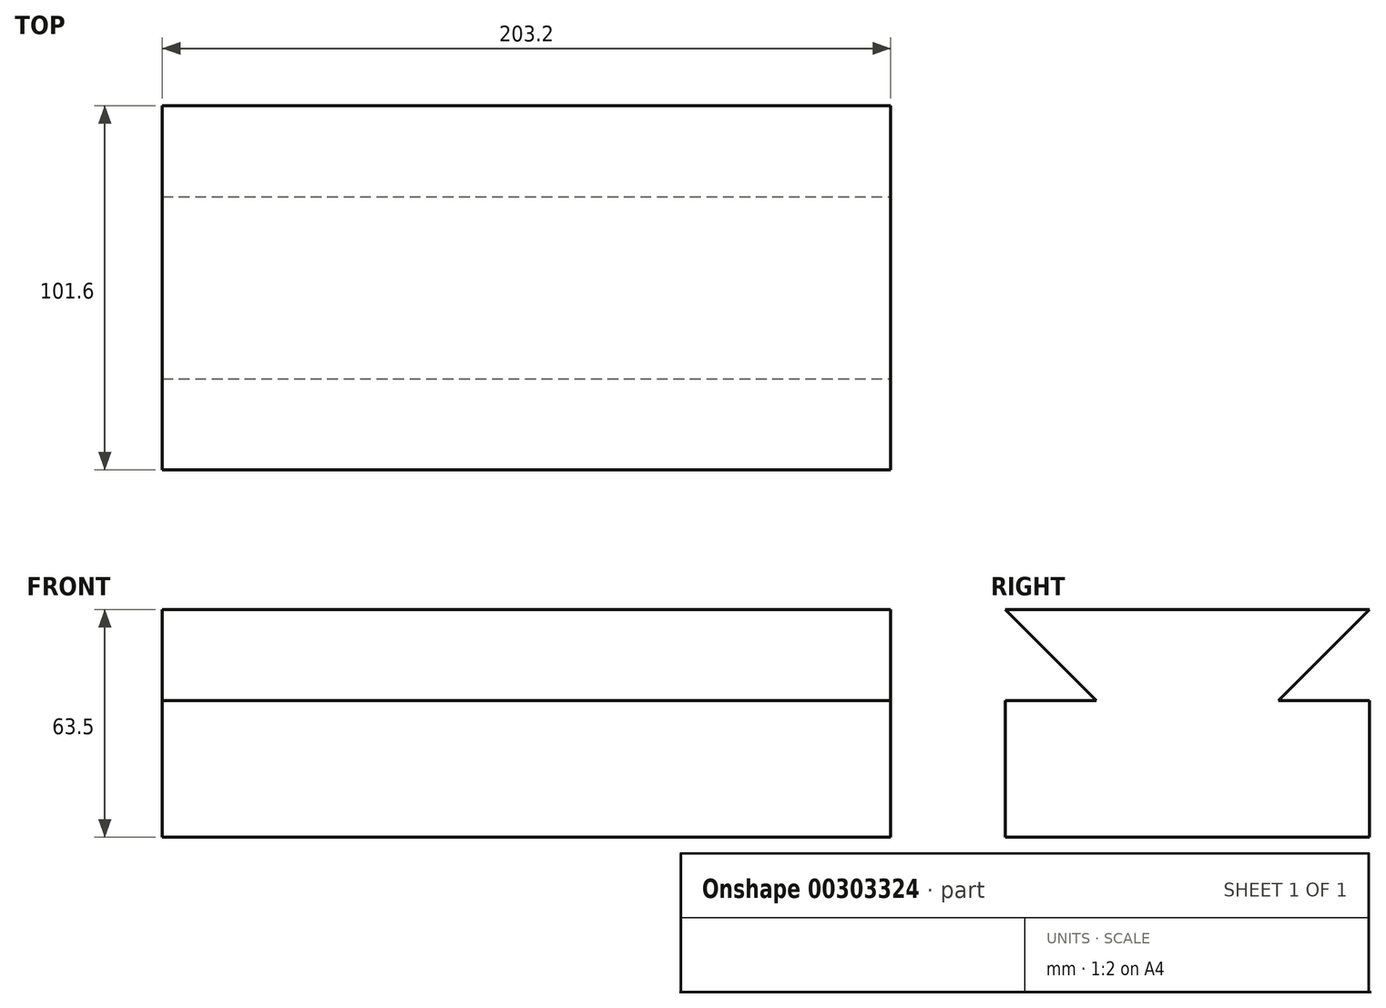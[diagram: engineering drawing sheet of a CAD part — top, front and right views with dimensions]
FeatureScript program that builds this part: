
annotation { "Feature Type Name" : "Feature", "Feature Type Description" : "" }
export const myFeature = defineFeature(function(context is Context, id is Id, definition is map)
    precondition{}
    {
        {
            var Q0;
            Q0=qCreatedBy(makeId("Right.planeOp"),FACE);
            var sketch = newSketch(context, id + "F0", { "sketchPlane" : qUnion([Q0])});
            skLineSegment(sketch, "E0.bottom", {"start": v(-35.6, 3.73) * mm, "end": v(66, 3.73) * mm});
            skLineSegment(sketch, "E0.top", {"start": v(-35.6, -59.77) * mm, "end": v(66, -59.77) * mm});
            skLineSegment(sketch, "E0.left", {"start": v(-35.6, 3.73) * mm, "end": v(-35.6, -59.77) * mm});
            skLineSegment(sketch, "E0.right", {"start": v(66, 3.73) * mm, "end": v(66, -59.77) * mm});
            skLineSegment(sketch, "E1", {"start": v(-35.6, 3.73) * mm, "end": v(-10.2, -21.67) * mm});
            skLineSegment(sketch, "E2", {"start": v(-10.2, -21.67) * mm, "end": v(-35.6, -21.67) * mm});
            skLineSegment(sketch, "E3", {"start": v(66, 3.73) * mm, "end": v(40.6, -21.67) * mm});
            skLineSegment(sketch, "E4", {"start": v(40.6, -21.67) * mm, "end": v(66, -21.67) * mm});
            skSolve(sketch);
        }
        {
            var Q0;
            Q0=makeQuery(id+"F0.imprint","IMPRINT",FACE,{"disambiguationData":[TD([[makeQuery(id+"F0.imprint","IMPRINT",EDGE,{"derivedFrom":sQuery(id+"F0.wireOp",EDGE,"E0.bottom")}),-1.0]])]});
            extrude(context, id + "F1", {"entities" : qUnion([Q0]), "oppositeDirection" : true, "depth" : 203.2 * mm});
        }
    });
